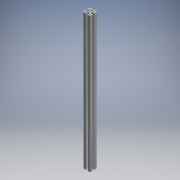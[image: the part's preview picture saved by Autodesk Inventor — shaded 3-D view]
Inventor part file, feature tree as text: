
AUTODESK INVENTOR PART (.ipt)
format: ipt  version: 2019 (Build 230136000, 136)  size: 310,784 bytes
history: native  units: mm
features: other x4, extrude x1, sketch x1, reference x1
ambient origin geometry x8: Origin, YZ Plane, XZ Plane, XY Plane, X Axis, Y Axis, Z Axis, Center Point
bodies: Body1 (feature_tree)
feature tree (7):
  other  "솔리드1"
  extrude  "돌출1"  Depth=600.0mm TaperAngle=0.0deg
  sketch  "스케치1"
  reference  "참조1"
  other  "<userpath>\Documents\Inventor\Projects\2019_CapstoneDesign\Body.iam"
  other  "Body.iam"
  other  "Propile_800:3"
